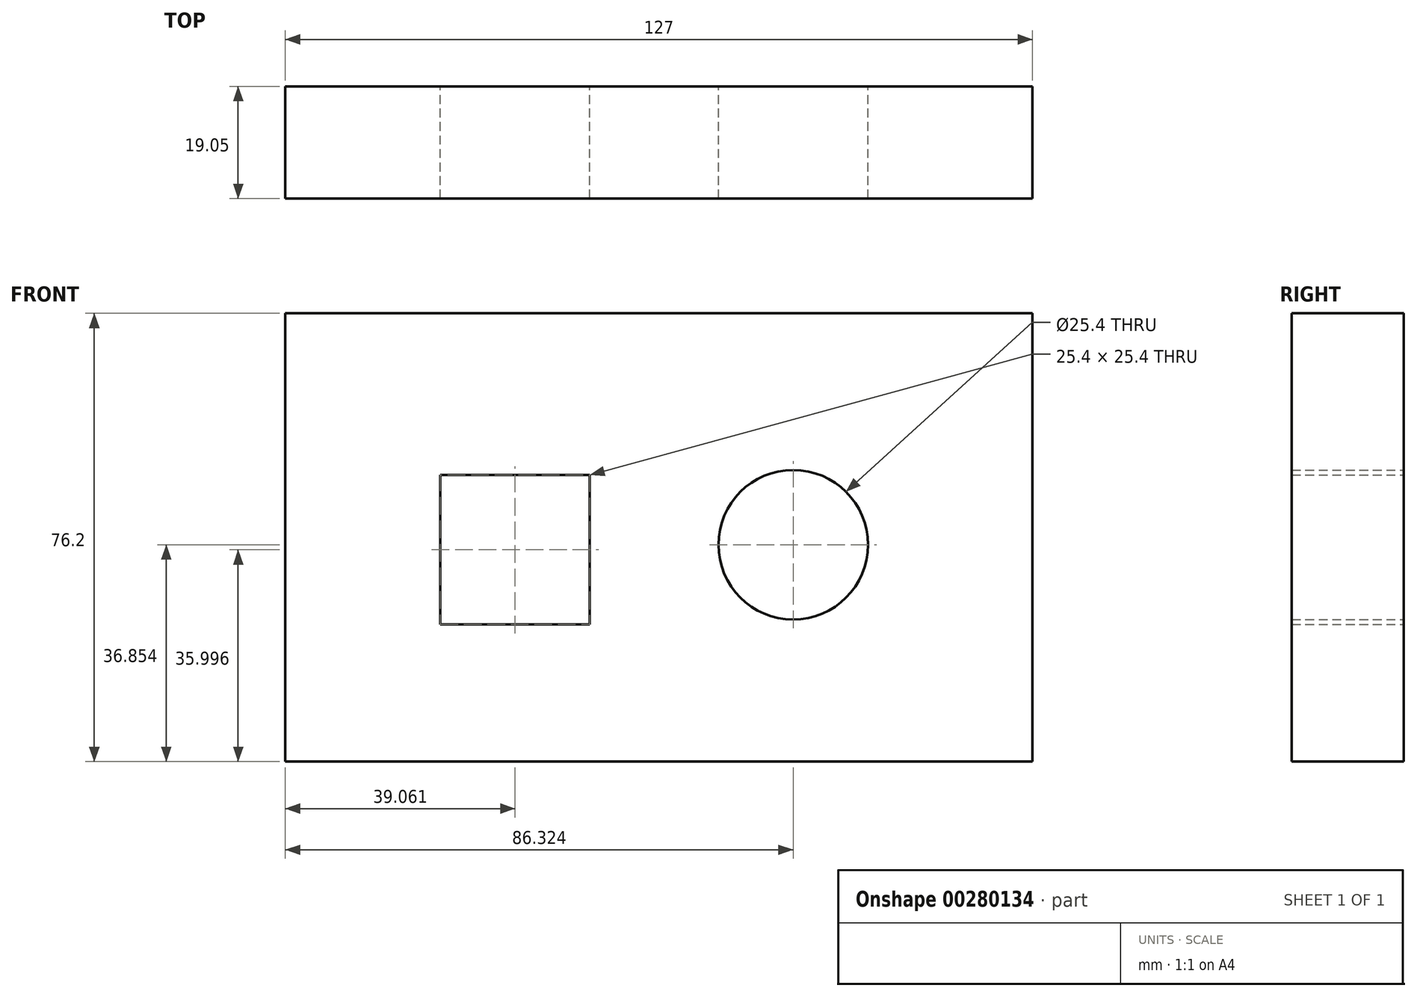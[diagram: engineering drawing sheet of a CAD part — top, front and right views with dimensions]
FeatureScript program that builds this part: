
annotation { "Feature Type Name" : "Feature", "Feature Type Description" : "" }
export const myFeature = defineFeature(function(context is Context, id is Id, definition is map)
    precondition{}
    {
        {
            var Q0;
            Q0=qCreatedBy(makeId("Front.planeOp"),FACE);
            var sketch = newSketch(context, id + "F0", { "sketchPlane" : qUnion([Q0])});
            skLineSegment(sketch, "E0.bottom", {"start": v(0, 0) * mm, "end": v(-127, 0) * mm});
            skLineSegment(sketch, "E0.top", {"start": v(0, 76.2) * mm, "end": v(-127, 76.2) * mm});
            skLineSegment(sketch, "E0.left", {"start": v(0, 0) * mm, "end": v(0, 76.2) * mm});
            skLineSegment(sketch, "E0.right", {"start": v(-127, 0) * mm, "end": v(-127, 76.2) * mm});
            skLineSegment(sketch, "E1.bottom", {"start": v(-100.64, 48.7) * mm, "end": v(-75.24, 48.7) * mm});
            skLineSegment(sketch, "E1.top", {"start": v(-100.64, 23.3) * mm, "end": v(-75.24, 23.3) * mm});
            skLineSegment(sketch, "E1.left", {"start": v(-100.64, 48.7) * mm, "end": v(-100.64, 23.3) * mm});
            skLineSegment(sketch, "E1.right", {"start": v(-75.24, 48.7) * mm, "end": v(-75.24, 23.3) * mm});
            skCircle(sketch, "E2", {"center": v(-40.68, 36.85) * mm, "radius": 12.7 * mm});
            skSolve(sketch);
        }
        {
            var Q0;
            Q0=makeQuery(id+"F0.imprint","IMPRINT",FACE,{"disambiguationData":[TD([[makeQuery(id+"F0.imprint","IMPRINT",EDGE,{"derivedFrom":sQuery(id+"F0.wireOp",EDGE,"E0.bottom")}),-1.0]])]});
            extrude(context, id + "F1", {"entities" : qUnion([Q0]), "depth" : 19.05 * mm});
        }
    });
